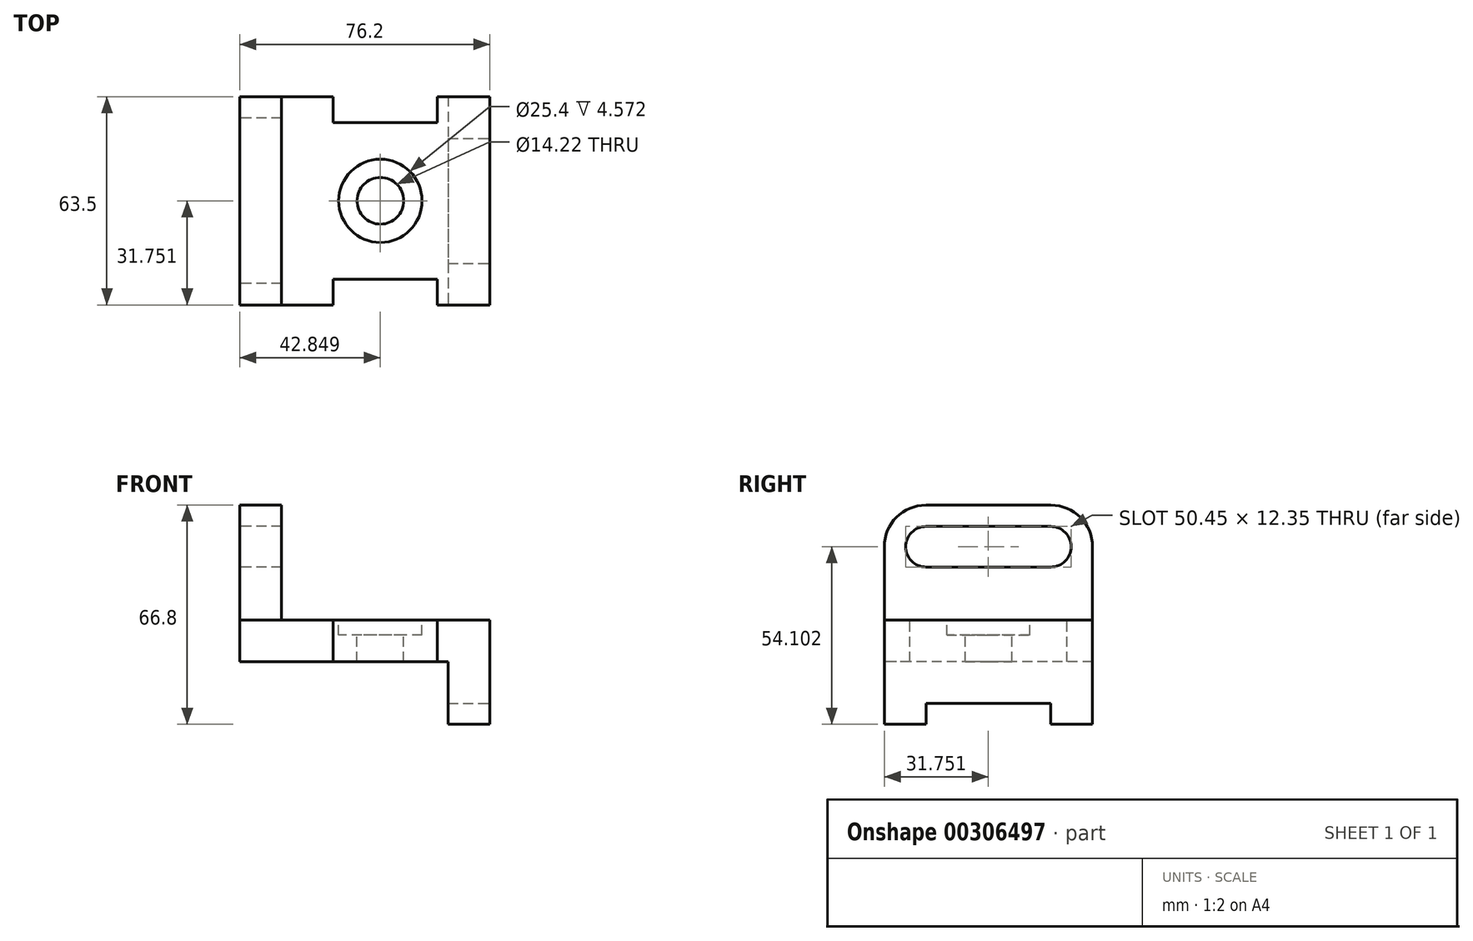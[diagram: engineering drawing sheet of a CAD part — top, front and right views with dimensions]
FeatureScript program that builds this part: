
annotation { "Feature Type Name" : "Feature", "Feature Type Description" : "" }
export const myFeature = defineFeature(function(context is Context, id is Id, definition is map)
    precondition{}
    {
        {
            var Q0;
            Q0=qCreatedBy(makeId("Right.planeOp"),FACE);
            var sketch = newSketch(context, id + "F0", { "sketchPlane" : qUnion([Q0])});
            skLineSegment(sketch, "E0", {"start": v(-40.46, 31.75) * mm, "end": v(-40.46, 0) * mm});
            skLineSegment(sketch, "E1", {"start": v(-40.46, 0) * mm, "end": v(23.04, 0) * mm});
            skLineSegment(sketch, "E2", {"start": v(23.04, 0) * mm, "end": v(23.04, 31.75) * mm});
            skLineSegment(sketch, "E3", {"start": v(-40.46, 31.75) * mm, "end": v(23.04, 31.75) * mm});
            skLineSegment(sketch, "E4", {"start": v(-40.46, 31.75) * mm, "end": v(-40.46, 54.1) * mm});
            skLineSegment(sketch, "E5", {"start": v(23.04, 31.75) * mm, "end": v(23.04, 54.1) * mm});
            skArc(sketch, "E6", {"start": v(23.04, 54.1) * mm, "mid": v(19.32, 63.08) * mm, "end": v(10.34, 66.8) * mm});
            skArc(sketch, "E7", {"start": v(-40.46, 54.1) * mm, "mid": v(-36.74, 63.08) * mm, "end": v(-27.76, 66.8) * mm});
            skLineSegment(sketch, "E8", {"start": v(-27.76, 66.8) * mm, "end": v(10.34, 66.8) * mm});
            skArc(sketch, "E9", {"start": v(-27.76, 60.28) * mm, "mid": v(-33.93, 54.1) * mm, "end": v(-27.76, 47.93) * mm});
            skArc(sketch, "E10", {"start": v(10.34, 60.28) * mm, "mid": v(16.52, 54.1) * mm, "end": v(10.34, 47.93) * mm});
            skLineSegment(sketch, "E11", {"start": v(-27.76, 60.28) * mm, "end": v(10.34, 60.28) * mm});
            skLineSegment(sketch, "E12", {"start": v(-27.76, 47.93) * mm, "end": v(10.34, 47.93) * mm});
            skSolve(sketch);
        }
        {
            var Q0;
            Q0=makeQuery(id+"F0.imprint","IMPRINT",FACE,{"disambiguationData":[TD([[makeQuery(id+"F0.imprint","IMPRINT",EDGE,{"derivedFrom":sQuery(id+"F0.wireOp",EDGE,"E0")}),1.0]])]});
            extrude(context, id + "F1", {"entities" : qUnion([Q0]), "depth" : 76.2 * mm});
        }
        {
            var Q0;
            Q0=makeQuery(id+"F0.imprint","IMPRINT",FACE,{"disambiguationData":[TD([[makeQuery(id+"F0.imprint","IMPRINT",EDGE,{"derivedFrom":sQuery(id+"F0.wireOp",EDGE,"E3")}),1.0]])]});
            extrude(context, id + "F2", {"entities" : qUnion([Q0]), "depth" : 12.7 * mm});
        }
        {
            var Q0;
            Q0=makeQuery(id+"F1.opExtrude","CAP_FACE",FACE,{"disambiguationData":[OSD([sQuery(id+"F0.wireOp",EDGE,"E0"),sQuery(id+"F0.wireOp",EDGE,"E1"),sQuery(id+"F0.wireOp",EDGE,"E2"),sQuery(id+"F0.wireOp",EDGE,"E3")])],"isStart":false});
            var sketch = newSketch(context, id + "F3", { "sketchPlane" : qUnion([Q0])});
            skLineSegment(sketch, "E13", {"start": v(-27.76, 6.35) * mm, "end": v(-27.76, 0) * mm});
            skLineSegment(sketch, "E14", {"start": v(-27.76, 0) * mm, "end": v(10.34, 0) * mm});
            skLineSegment(sketch, "E15", {"start": v(10.34, 0) * mm, "end": v(10.34, 6.35) * mm});
            skLineSegment(sketch, "E16", {"start": v(10.34, 6.35) * mm, "end": v(-27.76, 6.35) * mm});
            skSolve(sketch);
        }
        {
            var Q0;
            Q0 = qSketchRegion(id + "F3", true);
            extrude(context, id + "F4", {"entities" : qUnion([Q0]), "operationType" : NewBodyOperationType.REMOVE, "endBound" : BoundingType.THROUGH_ALL, "oppositeDirection" : true, "depth" : 25.4 * mm});
        }
        {
            var Q0;
            Q0=makeQuery(id+"F1.opExtrude","SWEPT_FACE",FACE,{"disambiguationData":[OSD([sQuery(id+"F0.wireOp",EDGE,"E3")])]});
            var sketch = newSketch(context, id + "F5", { "sketchPlane" : qUnion([Q0])});
            skLineSegment(sketch, "E17", {"start": v(28.45, -32.59) * mm, "end": v(28.45, -40.46) * mm});
            skLineSegment(sketch, "E18", {"start": v(28.45, -40.46) * mm, "end": v(60.2, -40.46) * mm});
            skLineSegment(sketch, "E19", {"start": v(60.2, -40.46) * mm, "end": v(60.2, -32.59) * mm});
            skLineSegment(sketch, "E20", {"start": v(60.2, -32.59) * mm, "end": v(28.45, -32.59) * mm});
            skLineSegment(sketch, "E21", {"start": v(28.45, 23.04) * mm, "end": v(28.45, 15.17) * mm});
            skLineSegment(sketch, "E22", {"start": v(28.45, 15.17) * mm, "end": v(60.2, 15.17) * mm});
            skLineSegment(sketch, "E23", {"start": v(60.2, 15.17) * mm, "end": v(60.2, 23.04) * mm});
            skLineSegment(sketch, "E24", {"start": v(28.45, 23.04) * mm, "end": v(60.2, 23.04) * mm});
            skSolve(sketch);
        }
        {
            var Q0;
            Q0=makeQuery(id+"F1.opExtrude","SWEPT_FACE",FACE,{"disambiguationData":[OSD([sQuery(id+"F0.wireOp",EDGE,"E0")])]});
            var sketch = newSketch(context, id + "F6", { "sketchPlane" : qUnion([Q0])});
            skLineSegment(sketch, "E25", {"start": v(63.5, 19.05) * mm, "end": v(63.5, 0) * mm});
            skLineSegment(sketch, "E26", {"start": v(63.5, 19.05) * mm, "end": v(0, 19.05) * mm});
            skLineSegment(sketch, "E27", {"start": v(63.5, 0) * mm, "end": v(0, 0) * mm});
            skLineSegment(sketch, "E28", {"start": v(0, 0) * mm, "end": v(0, 19.05) * mm});
            skSolve(sketch);
        }
        {
            var Q0;
            Q0 = qSketchRegion(id + "F6", true);
            extrude(context, id + "F7", {"entities" : qUnion([Q0]), "operationType" : NewBodyOperationType.REMOVE, "oppositeDirection" : true, "depth" : 63.5 * mm});
        }
        {
            var Q0;
            Q0 = qSketchRegion(id + "F5", true);
            extrude(context, id + "F8", {"entities" : qUnion([Q0]), "operationType" : NewBodyOperationType.REMOVE, "oppositeDirection" : true, "depth" : 25.4 * mm});
        }
        {
            var Q0;
            Q0=makeQuery(id+"F1.opExtrude","SWEPT_FACE",FACE,{"disambiguationData":[OSD([sQuery(id+"F0.wireOp",EDGE,"E3")])]});
            var sketch = newSketch(context, id + "F9", { "sketchPlane" : qUnion([Q0])});
            skCircle(sketch, "E29", {"center": v(42.85, -8.7) * mm, "radius": 12.7 * mm});
            skCircle(sketch, "E30", {"center": v(42.85, -8.7) * mm, "radius": 7.11 * mm});
            skSolve(sketch);
        }
        {
            var Q0;
            Q0=makeQuery(id+"F9.imprint","IMPRINT",FACE,{"disambiguationData":[TD([[makeQuery(id+"F9.imprint","IMPRINT",EDGE,{"derivedFrom":sQuery(id+"F9.wireOp",EDGE,"E29")}),1.0]])]});
            extrude(context, id + "F10", {"entities" : qUnion([Q0]), "operationType" : NewBodyOperationType.REMOVE, "oppositeDirection" : true, "depth" : 4.57 * mm});
        }
        {
            var Q0;
            Q0=makeQuery(id+"F10.boolean.opBoolean","SPLIT",FACE,{"disambiguationData":[TD([makeQuery(id+"F10.opExtrude","SWEPT_FACE",FACE,{"disambiguationData":[OSD([sQuery(id+"F9.wireOp",EDGE,"E30")])]})])],"derivedFrom":makeQuery(id+"F1.opExtrude","SWEPT_FACE",FACE,{"disambiguationData":[OSD([sQuery(id+"F0.wireOp",EDGE,"E3")])]})});
            extrude(context, id + "F11", {"entities" : qUnion([Q0]), "operationType" : NewBodyOperationType.REMOVE, "oppositeDirection" : true, "depth" : 25.4 * mm});
        }
    });
